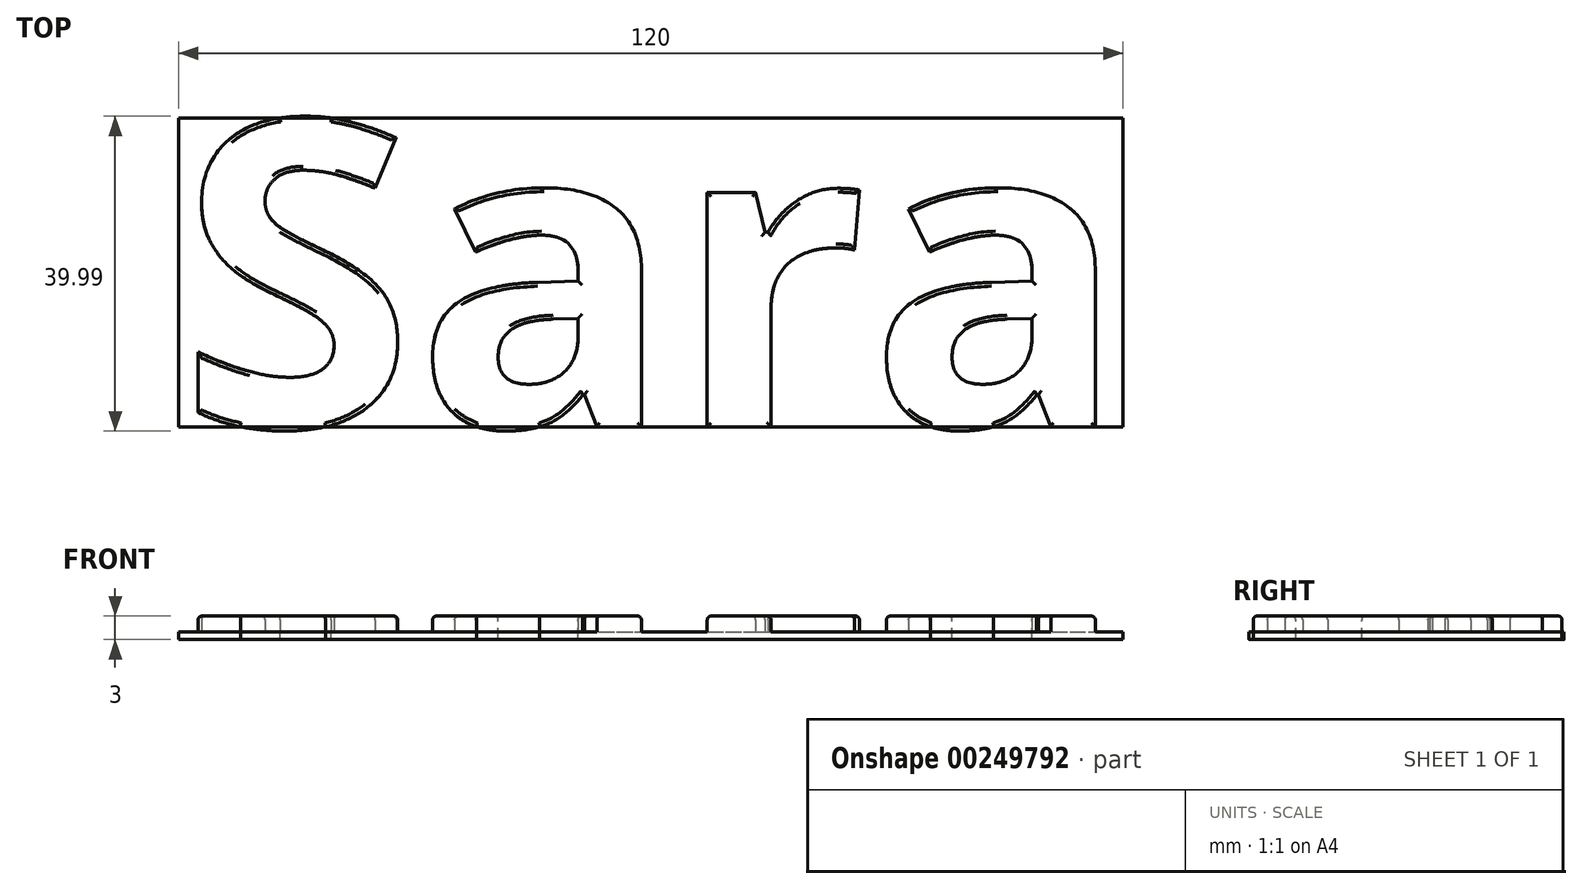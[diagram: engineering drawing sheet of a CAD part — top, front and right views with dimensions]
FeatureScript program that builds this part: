
annotation { "Feature Type Name" : "Feature", "Feature Type Description" : "" }
export const myFeature = defineFeature(function(context is Context, id is Id, definition is map)
    precondition{}
    {
        {
            var Q0;
            Q0=qCreatedBy(makeId("Top.planeOp"),FACE);
            var sketch = newSketch(context, id + "F0", { "sketchPlane" : qUnion([Q0])});
            skText(sketch, "E0", { "text": "Sara", "fontName": "OpenSans-Bold.ttf"});
            skLineSegment(sketch, "E1.bottom", {"start": v(0, 0) * mm, "end": v(120, 0) * mm});
            skLineSegment(sketch, "E1.top", {"start": v(0, 39.23) * mm, "end": v(120, 39.23) * mm});
            skLineSegment(sketch, "E1.left", {"start": v(0, 0) * mm, "end": v(0, 39.23) * mm});
            skLineSegment(sketch, "E1.right", {"start": v(120, 0) * mm, "end": v(120, 39.23) * mm});
            skLineSegment(sketch, "E2", {"start": v(120, 0) * mm, "end": v(116.42, 0) * mm});
            const initialGuessF0  = {"E0": [0, 0, 1, 0, 0.03923]};
            skSetInitialGuess(sketch, initialGuessF0);
            skSolve(sketch);
        }
        {
            var Q0;
            Q0 = qSketchRegion(id + "F0", true);
            extrude(context, id + "F1", {"entities" : qUnion([Q0]), "oppositeDirection" : true, "depth" : 1 * mm});
        }
        {
            var Q0;
            {var subQ11=sQuery(id+"F0.wireOp",EDGE,"E0.sketch_text.stroke-0");Q0=makeQuery(id+"F0.imprint","IMPRINT",FACE,{"disambiguationData":[TD([[makeQuery(id+"F0.imprint","IMPRINT",EDGE,{"derivedFrom":subQ11}),-1.0]])]});}
            var Q1;
            {var subQ8=sQuery(id+"F0.wireOp",EDGE,"E0.sketch_text.stroke-28");Q1=makeQuery(id+"F0.imprint","IMPRINT",FACE,{"disambiguationData":[TD([[makeQuery(id+"F0.imprint","IMPRINT",EDGE,{"derivedFrom":subQ8}),-1.0]])]});}
            var Q2;
            Q2=makeQuery(id+"F0.imprint","IMPRINT",FACE,{"disambiguationData":[TD([[makeQuery(id+"F0.imprint","IMPRINT",EDGE,{"derivedFrom":sQuery(id+"F0.wireOp",EDGE,"E0.sketch_text.stroke-53")}),-1.0]])]});
            var Q3;
            {var subQ8=sQuery(id+"F0.wireOp",EDGE,"E0.sketch_text.stroke-66");Q3=makeQuery(id+"F0.imprint","IMPRINT",FACE,{"disambiguationData":[TD([[makeQuery(id+"F0.imprint","IMPRINT",EDGE,{"derivedFrom":subQ8}),-1.0]])]});}
            extrude(context, id + "F2", {"entities" : qUnion([Q0, Q1, Q2, Q3]), "operationType" : NewBodyOperationType.ADD, "depth" : 2 * mm});
        }
        {
            var Q0;
            Q0=makeQuery(id+"F2.opExtrude","CAP_FACE",FACE,{"disambiguationData":[OSD([sQuery(id+"F0.wireOp",EDGE,"E0.sketch_text.stroke-0"),sQuery(id+"F0.wireOp",EDGE,"E0.sketch_text.stroke-1"),sQuery(id+"F0.wireOp",EDGE,"E0.sketch_text.stroke-2"),sQuery(id+"F0.wireOp",EDGE,"E0.sketch_text.stroke-3"),sQuery(id+"F0.wireOp",EDGE,"E0.sketch_text.stroke-4"),sQuery(id+"F0.wireOp",EDGE,"E0.sketch_text.stroke-5"),sQuery(id+"F0.wireOp",EDGE,"E0.sketch_text.stroke-6"),sQuery(id+"F0.wireOp",EDGE,"E0.sketch_text.stroke-7"),sQuery(id+"F0.wireOp",EDGE,"E0.sketch_text.stroke-8"),sQuery(id+"F0.wireOp",EDGE,"E0.sketch_text.stroke-9"),sQuery(id+"F0.wireOp",EDGE,"E0.sketch_text.stroke-10"),sQuery(id+"F0.wireOp",EDGE,"E0.sketch_text.stroke-11"),sQuery(id+"F0.wireOp",EDGE,"E0.sketch_text.stroke-12"),sQuery(id+"F0.wireOp",EDGE,"E0.sketch_text.stroke-13"),sQuery(id+"F0.wireOp",EDGE,"E0.sketch_text.stroke-14"),sQuery(id+"F0.wireOp",EDGE,"E0.sketch_text.stroke-15"),sQuery(id+"F0.wireOp",EDGE,"E0.sketch_text.stroke-16"),sQuery(id+"F0.wireOp",EDGE,"E0.sketch_text.stroke-17"),sQuery(id+"F0.wireOp",EDGE,"E0.sketch_text.stroke-18"),sQuery(id+"F0.wireOp",EDGE,"E0.sketch_text.stroke-19"),sQuery(id+"F0.wireOp",EDGE,"E0.sketch_text.stroke-20"),sQuery(id+"F0.wireOp",EDGE,"E0.sketch_text.stroke-21"),sQuery(id+"F0.wireOp",EDGE,"E0.sketch_text.stroke-22"),sQuery(id+"F0.wireOp",EDGE,"E0.sketch_text.stroke-23"),sQuery(id+"F0.wireOp",EDGE,"E0.sketch_text.stroke-24"),sQuery(id+"F0.wireOp",EDGE,"E0.sketch_text.stroke-25"),sQuery(id+"F0.wireOp",EDGE,"E0.sketch_text.stroke-26"),sQuery(id+"F0.wireOp",EDGE,"E0.sketch_text.stroke-27"),sQuery(id+"F0.wireOp",EDGE,"E1.bottom"),sQuery(id+"F0.wireOp",EDGE,"E1.top")])],"isStart":false});
            var Q1;
            Q1=makeQuery(id+"F2.opExtrude","CAP_FACE",FACE,{"disambiguationData":[OSD([sQuery(id+"F0.wireOp",EDGE,"E0.sketch_text.stroke-28"),sQuery(id+"F0.wireOp",EDGE,"E0.sketch_text.stroke-29"),sQuery(id+"F0.wireOp",EDGE,"E0.sketch_text.stroke-30"),sQuery(id+"F0.wireOp",EDGE,"E0.sketch_text.stroke-31"),sQuery(id+"F0.wireOp",EDGE,"E0.sketch_text.stroke-32"),sQuery(id+"F0.wireOp",EDGE,"E0.sketch_text.stroke-33"),sQuery(id+"F0.wireOp",EDGE,"E0.sketch_text.stroke-34"),sQuery(id+"F0.wireOp",EDGE,"E0.sketch_text.stroke-35"),sQuery(id+"F0.wireOp",EDGE,"E0.sketch_text.stroke-36"),sQuery(id+"F0.wireOp",EDGE,"E0.sketch_text.stroke-37"),sQuery(id+"F0.wireOp",EDGE,"E0.sketch_text.stroke-38"),sQuery(id+"F0.wireOp",EDGE,"E0.sketch_text.stroke-39"),sQuery(id+"F0.wireOp",EDGE,"E0.sketch_text.stroke-40"),sQuery(id+"F0.wireOp",EDGE,"E0.sketch_text.stroke-41"),sQuery(id+"F0.wireOp",EDGE,"E0.sketch_text.stroke-42"),sQuery(id+"F0.wireOp",EDGE,"E0.sketch_text.stroke-43"),sQuery(id+"F0.wireOp",EDGE,"E0.sketch_text.stroke-44"),sQuery(id+"F0.wireOp",EDGE,"E0.sketch_text.stroke-46"),sQuery(id+"F0.wireOp",EDGE,"E0.sketch_text.stroke-47"),sQuery(id+"F0.wireOp",EDGE,"E0.sketch_text.stroke-48"),sQuery(id+"F0.wireOp",EDGE,"E0.sketch_text.stroke-49"),sQuery(id+"F0.wireOp",EDGE,"E0.sketch_text.stroke-50"),sQuery(id+"F0.wireOp",EDGE,"E0.sketch_text.stroke-51"),sQuery(id+"F0.wireOp",EDGE,"E0.sketch_text.stroke-52"),sQuery(id+"F0.wireOp",EDGE,"E1.bottom")])],"isStart":false});
            var Q2;
            Q2=makeQuery(id+"F2.opExtrude","CAP_FACE",FACE,{"disambiguationData":[OSD([sQuery(id+"F0.wireOp",EDGE,"E0.sketch_text.stroke-53"),sQuery(id+"F0.wireOp",EDGE,"E0.sketch_text.stroke-54"),sQuery(id+"F0.wireOp",EDGE,"E0.sketch_text.stroke-55"),sQuery(id+"F0.wireOp",EDGE,"E0.sketch_text.stroke-56"),sQuery(id+"F0.wireOp",EDGE,"E0.sketch_text.stroke-57"),sQuery(id+"F0.wireOp",EDGE,"E0.sketch_text.stroke-58"),sQuery(id+"F0.wireOp",EDGE,"E0.sketch_text.stroke-60"),sQuery(id+"F0.wireOp",EDGE,"E0.sketch_text.stroke-61"),sQuery(id+"F0.wireOp",EDGE,"E0.sketch_text.stroke-62"),sQuery(id+"F0.wireOp",EDGE,"E0.sketch_text.stroke-63"),sQuery(id+"F0.wireOp",EDGE,"E0.sketch_text.stroke-64"),sQuery(id+"F0.wireOp",EDGE,"E0.sketch_text.stroke-65"),sQuery(id+"F0.wireOp",EDGE,"E1.bottom")])],"isStart":false});
            var Q3;
            Q3=makeQuery(id+"F2.opExtrude","CAP_FACE",FACE,{"disambiguationData":[OSD([sQuery(id+"F0.wireOp",EDGE,"E0.sketch_text.stroke-66"),sQuery(id+"F0.wireOp",EDGE,"E0.sketch_text.stroke-67"),sQuery(id+"F0.wireOp",EDGE,"E0.sketch_text.stroke-68"),sQuery(id+"F0.wireOp",EDGE,"E0.sketch_text.stroke-69"),sQuery(id+"F0.wireOp",EDGE,"E0.sketch_text.stroke-70"),sQuery(id+"F0.wireOp",EDGE,"E0.sketch_text.stroke-71"),sQuery(id+"F0.wireOp",EDGE,"E0.sketch_text.stroke-72"),sQuery(id+"F0.wireOp",EDGE,"E0.sketch_text.stroke-73"),sQuery(id+"F0.wireOp",EDGE,"E0.sketch_text.stroke-74"),sQuery(id+"F0.wireOp",EDGE,"E0.sketch_text.stroke-75"),sQuery(id+"F0.wireOp",EDGE,"E0.sketch_text.stroke-76"),sQuery(id+"F0.wireOp",EDGE,"E0.sketch_text.stroke-77"),sQuery(id+"F0.wireOp",EDGE,"E0.sketch_text.stroke-78"),sQuery(id+"F0.wireOp",EDGE,"E0.sketch_text.stroke-79"),sQuery(id+"F0.wireOp",EDGE,"E0.sketch_text.stroke-80"),sQuery(id+"F0.wireOp",EDGE,"E0.sketch_text.stroke-81"),sQuery(id+"F0.wireOp",EDGE,"E0.sketch_text.stroke-82"),sQuery(id+"F0.wireOp",EDGE,"E0.sketch_text.stroke-84"),sQuery(id+"F0.wireOp",EDGE,"E0.sketch_text.stroke-85"),sQuery(id+"F0.wireOp",EDGE,"E0.sketch_text.stroke-86"),sQuery(id+"F0.wireOp",EDGE,"E0.sketch_text.stroke-87"),sQuery(id+"F0.wireOp",EDGE,"E0.sketch_text.stroke-88"),sQuery(id+"F0.wireOp",EDGE,"E0.sketch_text.stroke-89"),sQuery(id+"F0.wireOp",EDGE,"E0.sketch_text.stroke-90"),sQuery(id+"F0.wireOp",EDGE,"E1.bottom")])],"isStart":false});
            fillet(context, id + "F3", {"entities" : qUnion([Q0, Q1, Q2, Q3]), "radius" : 0.5 * mm, "tangentPropagation" : true, "allowEdgeOverflow" : false});
        }
    });
